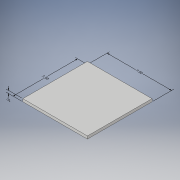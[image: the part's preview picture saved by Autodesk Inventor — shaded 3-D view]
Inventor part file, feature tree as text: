
AUTODESK INVENTOR PART (.ipt)
format: ipt  version: 2019 (Build 230136000, 136)  size: 100,864 bytes
history: native  units: in
note: dims shown in document units (in); Inventor stores cm internally (conversion verified against a paired STEP export)
features: other x4, extrude x1, sketch x1
ambient origin geometry x8: Origin, YZ Plane, XZ Plane, XY Plane, X Axis, Y Axis, Z Axis, Center Point
bodies: Solid1 (feature_tree)
feature tree (6):
  other  "Annotations"
  extrude  "Extrusion1"  Depth=7.5in
  sketch  "Sketch1"  dims[d0=7.5in d1=7.5in d2=0.3125in d3=0.0in d10=0.0in d11=0.3937in d12=0.3125in d4=0.0in d5=0.3937in d6=7.5in d7=0.0in d8=0.3937in d9=7.5in]
  other  "Linear Dimension 1"
  other  "Linear Dimension 2"
  other  "Linear Dimension 3"
